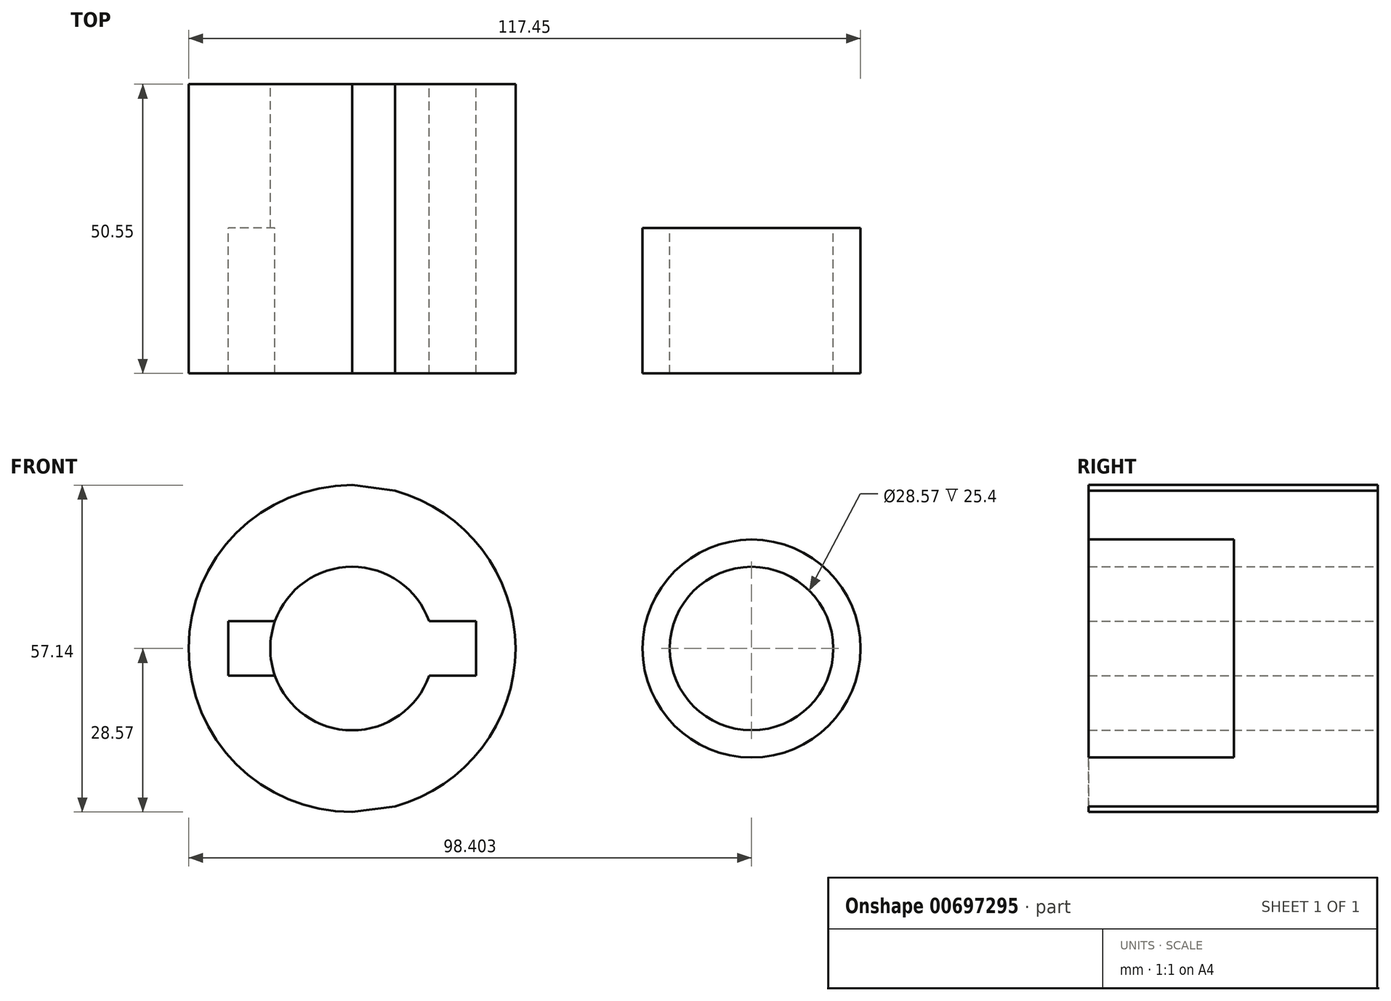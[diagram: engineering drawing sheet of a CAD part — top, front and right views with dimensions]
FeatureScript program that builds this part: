
annotation { "Feature Type Name" : "Feature", "Feature Type Description" : "" }
export const myFeature = defineFeature(function(context is Context, id is Id, definition is map)
    precondition{}
    {
        {
            var Q0;
            Q0=qCreatedBy(makeId("Front.planeOp"),FACE);
            var sketch = newSketch(context, id + "F0", { "sketchPlane" : qUnion([Q0])});
            skCircle(sketch, "E0", {"center": v(0, 0) * mm, "radius": 28.58 * mm});
            skCircle(sketch, "E1", {"center": v(69.83, 0) * mm, "radius": 19.05 * mm});
            skLineSegment(sketch, "E2", {"start": v(0, 28.58) * mm, "end": v(72.36, 18.88) * mm});
            skLineSegment(sketch, "E3", {"start": v(0, -28.58) * mm, "end": v(72.36, -18.88) * mm});
            skCircle(sketch, "E4", {"center": v(0, 0) * mm, "radius": 14.29 * mm});
            skCircle(sketch, "E5", {"center": v(69.83, 0) * mm, "radius": 14.29 * mm});
            skLineSegment(sketch, "E6.bottom", {"start": v(21.66, -4.76) * mm, "end": v(-21.66, -4.76) * mm});
            skLineSegment(sketch, "E6.top", {"start": v(21.66, 4.76) * mm, "end": v(-21.66, 4.76) * mm});
            skLineSegment(sketch, "E6.left", {"start": v(21.66, -4.76) * mm, "end": v(21.66, 4.76) * mm});
            skLineSegment(sketch, "E6.right", {"start": v(-21.66, -4.76) * mm, "end": v(-21.66, 4.76) * mm});
            skSolve(sketch);
        }
        {
            var Q0;
            {var subQ0=sQuery(id+"F0.wireOp",EDGE,"E2");var subQ1=sQuery(id+"F0.wireOp",EDGE,"E0");var subQ2=makeQuery(id+"F0.imprint","INTERSECT",VERTEX,{"disambiguationData":[OD(0.0)],"derivedFrom":[subQ1,subQ0]});Q0=makeQuery(id+"F0.imprint","IMPRINT",FACE,{"disambiguationData":[TD([[makeQuery(id+"F0.imprint","IMPRINT",EDGE,{"disambiguationData":[TD([[subQ2,1.0]])],"derivedFrom":subQ1}),1.0]])]});}
            var Q1;
            {var subQ0=sQuery(id+"F0.wireOp",EDGE,"E3");var subQ1=sQuery(id+"F0.wireOp",EDGE,"E0");var subQ2=makeQuery(id+"F0.imprint","INTERSECT",VERTEX,{"disambiguationData":[OD(0.0)],"derivedFrom":[subQ1,subQ0]});Q1=makeQuery(id+"F0.imprint","IMPRINT",FACE,{"disambiguationData":[TD([[makeQuery(id+"F0.imprint","IMPRINT",EDGE,{"disambiguationData":[TD([[subQ2,-1.0]])],"derivedFrom":subQ1}),1.0]])]});}
            var Q2;
            {var subQ0=sQuery(id+"F0.wireOp",EDGE,"E2");var subQ1=sQuery(id+"F0.wireOp",EDGE,"E0");var subQ2=makeQuery(id+"F0.imprint","INTERSECT",VERTEX,{"disambiguationData":[OD(1.0)],"derivedFrom":[subQ1,subQ0]});Q2=makeQuery(id+"F0.imprint","IMPRINT",FACE,{"disambiguationData":[TD([[makeQuery(id+"F0.imprint","IMPRINT",EDGE,{"disambiguationData":[TD([[subQ2,1.0]])],"derivedFrom":subQ1}),-1.0]])]});}
            var Q3;
            Q3=makeQuery(id+"F0.imprint","IMPRINT",FACE,{"disambiguationData":[TD([[makeQuery(id+"F0.imprint","IMPRINT",EDGE,{"derivedFrom":sQuery(id+"F0.wireOp",EDGE,"E5")}),-1.0]])]});
            var Q4;
            {var subQ4=sQuery(id+"F0.wireOp",EDGE,"E6.left");Q4=makeQuery(id+"F0.imprint","IMPRINT",FACE,{"disambiguationData":[TD([[makeQuery(id+"F0.imprint","IMPRINT",EDGE,{"derivedFrom":subQ4}),-1.0]])]});}
            extrude(context, id + "F1", {"entities" : qUnion([Q0, Q1, Q2, Q3, Q4]), "depth" : 25.4 * mm, "offsetDistance" : 25.4 * mm});
        }
        {
            var Q0;
            {var subQ5=sQuery(id+"F0.wireOp",EDGE,"E6.right");Q0=makeQuery(id+"F0.imprint","IMPRINT",FACE,{"disambiguationData":[TD([[makeQuery(id+"F0.imprint","IMPRINT",EDGE,{"derivedFrom":subQ5}),-1.0]])]});}
            var Q1;
            {var subQ4=sQuery(id+"F0.wireOp",EDGE,"E6.left");Q1=makeQuery(id+"F0.imprint","IMPRINT",FACE,{"disambiguationData":[TD([[makeQuery(id+"F0.imprint","IMPRINT",EDGE,{"derivedFrom":subQ4}),-1.0]])]});}
            extrude(context, id + "F2", {"entities" : qUnion([Q0, Q1]), "operationType" : NewBodyOperationType.ADD, "oppositeDirection" : true, "depth" : 25.15 * mm, "offsetDistance" : 25.4 * mm});
        }
    });
